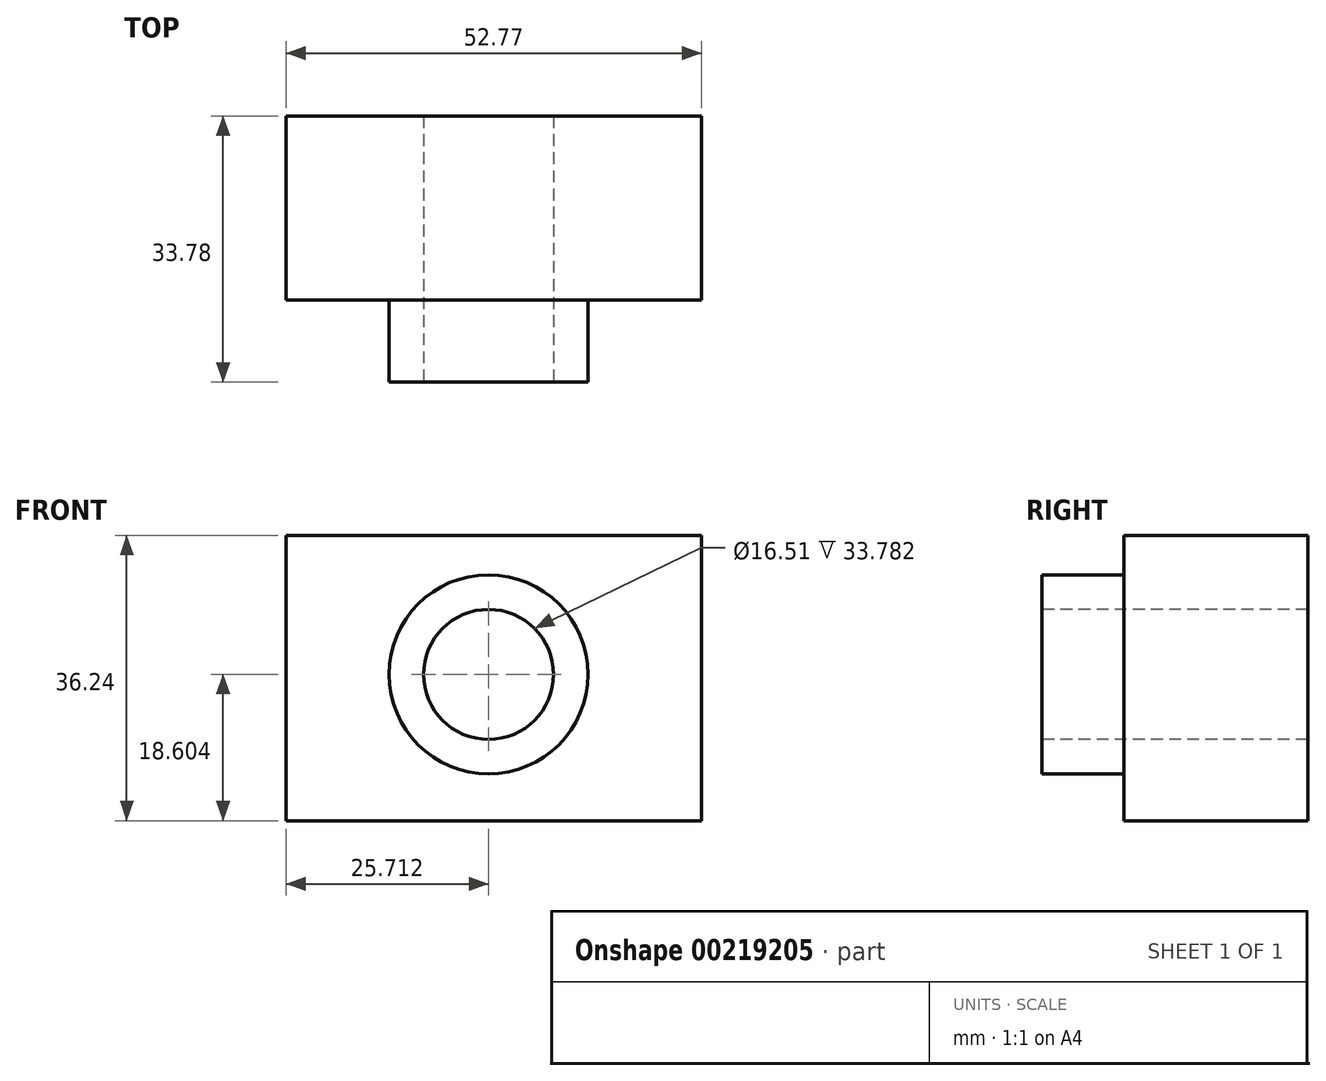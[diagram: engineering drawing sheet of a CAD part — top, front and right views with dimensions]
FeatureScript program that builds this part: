
annotation { "Feature Type Name" : "Feature", "Feature Type Description" : "" }
export const myFeature = defineFeature(function(context is Context, id is Id, definition is map)
    precondition{}
    {
        {
            var Q0;
            Q0=qCreatedBy(makeId("Front.planeOp"),FACE);
            var sketch = newSketch(context, id + "F0", { "sketchPlane" : qUnion([Q0])});
            skLineSegment(sketch, "E0.bottom", {"start": v(0, 0) * mm, "end": v(52.77, 0) * mm});
            skLineSegment(sketch, "E0.top", {"start": v(0, 36.24) * mm, "end": v(52.77, 36.24) * mm});
            skLineSegment(sketch, "E0.left", {"start": v(0, 0) * mm, "end": v(0, 36.24) * mm});
            skLineSegment(sketch, "E0.right", {"start": v(52.77, 0) * mm, "end": v(52.77, 36.24) * mm});
            skSolve(sketch);
        }
        {
            var Q0;
            Q0 = qSketchRegion(id + "F0", true);
            extrude(context, id + "F1", {"entities" : qUnion([Q0]), "depth" : 23.37 * mm});
        }
        {
            var Q0;
            Q0=makeQuery(id+"F1.opExtrude","CAP_FACE",FACE,{"disambiguationData":[OSD([sQuery(id+"F0.wireOp",EDGE,"E0.bottom"),sQuery(id+"F0.wireOp",EDGE,"E0.top"),sQuery(id+"F0.wireOp",EDGE,"E0.left"),sQuery(id+"F0.wireOp",EDGE,"E0.right")])],"isStart":false});
            var sketch = newSketch(context, id + "F2", { "sketchPlane" : qUnion([Q0])});
            skCircle(sketch, "E1", {"center": v(25.71, 18.6) * mm, "radius": 12.64 * mm});
            skSolve(sketch);
        }
        {
            var Q0;
            Q0=makeQuery(id+"F2.imprint","IMPRINT",FACE,{"disambiguationData":[TD([[makeQuery(id+"F2.imprint","IMPRINT",EDGE,{"derivedFrom":sQuery(id+"F2.wireOp",EDGE,"E1")}),1.0]])]});
            extrude(context, id + "F3", {"entities" : qUnion([Q0]), "operationType" : NewBodyOperationType.ADD, "depth" : 10.4 * mm});
        }
        {
            var Q0;
            Q0=makeQuery(id+"F3.opExtrude","CAP_FACE",FACE,{"disambiguationData":[OSD([sQuery(id+"F2.wireOp",EDGE,"E1")])],"isStart":false});
            var sketch = newSketch(context, id + "F4", { "sketchPlane" : qUnion([Q0])});
            skCircle(sketch, "E2", {"center": v(25.71, 18.6) * mm, "radius": 9.85 * mm});
            skSolve(sketch);
        }
        {
            var Q0;
            Q0=sQuery(id+"F4.wireOp",VERTEX,"E2.center");
            var Q1;
            Q1=makeQuery(id+"F1.opExtrude","SWEPT_BODY",BODY,{"disambiguationData":[OSD([sQuery(id+"F0.wireOp",EDGE,"E0.bottom"),sQuery(id+"F0.wireOp",EDGE,"E0.top"),sQuery(id+"F0.wireOp",EDGE,"E0.left"),sQuery(id+"F0.wireOp",EDGE,"E0.right")])]});
            hole(context, id + "F5", {"style" : HoleStyle.SIMPLE, "endStyle" : HoleEndStyle.THROUGH, "holeDiameter" : 16.5 * mm, "locations" : qUnion([Q0]), "scope" : qUnion([Q1]), "isTappedThrough" : true});
        }
    });
